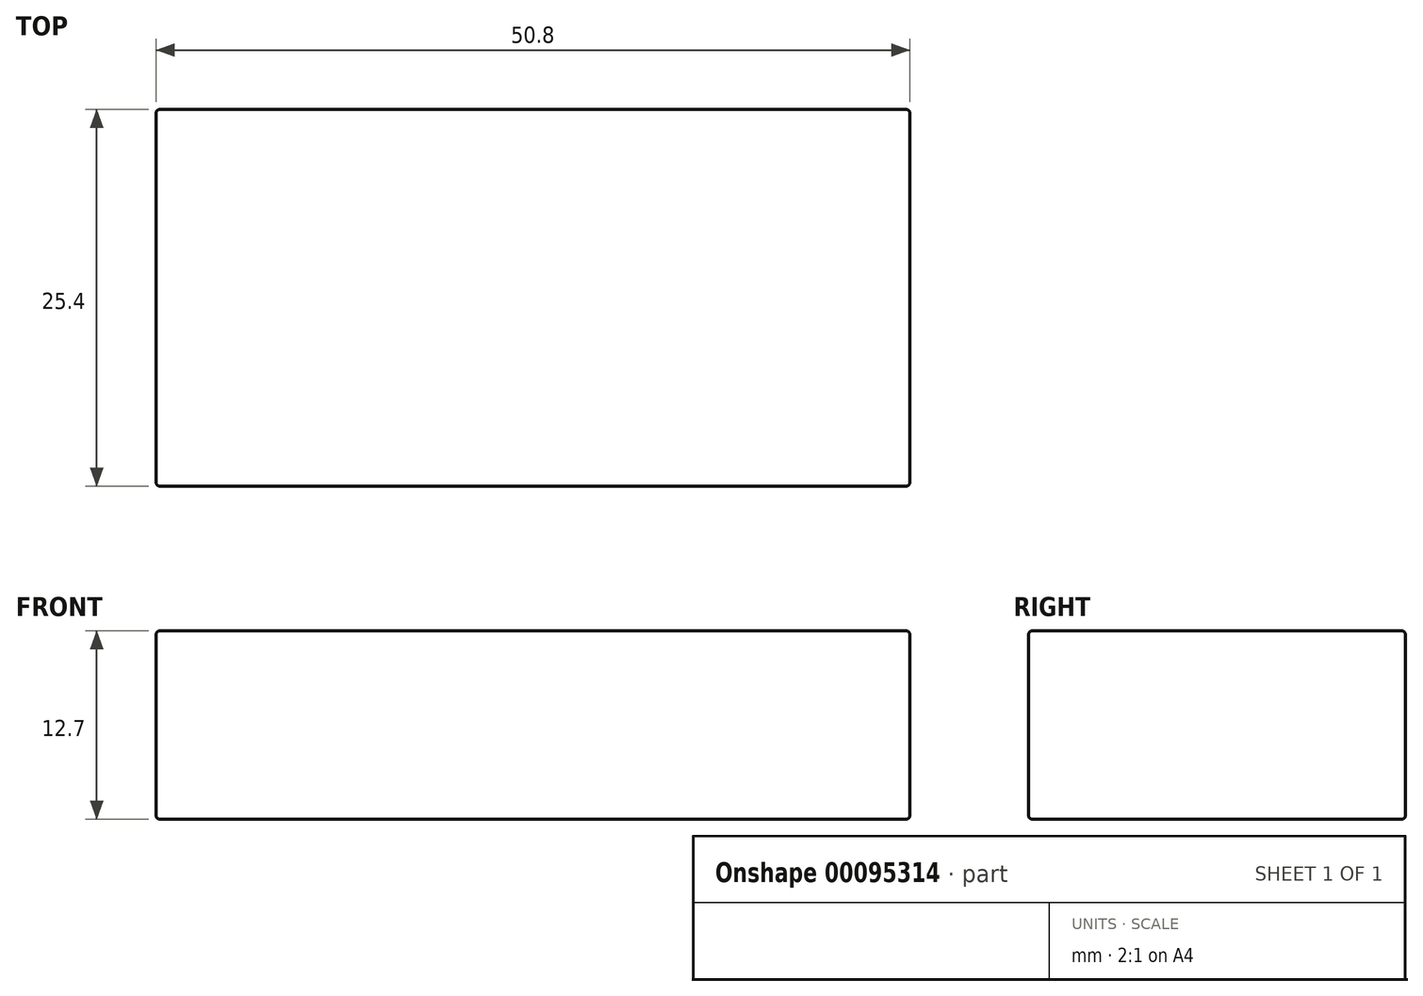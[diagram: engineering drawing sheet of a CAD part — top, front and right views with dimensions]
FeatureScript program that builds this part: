
annotation { "Feature Type Name" : "Feature", "Feature Type Description" : "" }
export const myFeature = defineFeature(function(context is Context, id is Id, definition is map)
    precondition{}
    {
        {
            var Q0;
            Q0=qCreatedBy(makeId("Front.planeOp"),FACE);
            var sketch = newSketch(context, id + "F0", { "sketchPlane" : qUnion([Q0])});
            skLineSegment(sketch, "E0.bottom", {"start": v(25.4, -6.35) * mm, "end": v(-25.4, -6.35) * mm});
            skLineSegment(sketch, "E0.top", {"start": v(25.4, 6.35) * mm, "end": v(-25.4, 6.35) * mm});
            skLineSegment(sketch, "E0.left", {"start": v(25.4, -6.35) * mm, "end": v(25.4, 6.35) * mm});
            skLineSegment(sketch, "E0.right", {"start": v(-25.4, -6.35) * mm, "end": v(-25.4, 6.35) * mm});
            skPoint(sketch, "E0.middle", {"position": v(0, 0) * mm});
            skSolve(sketch);
        }
        {
            var Q0;
            Q0=makeQuery(id+"F0.imprint","IMPRINT",FACE,{"disambiguationData":[TD([[makeQuery(id+"F0.imprint","IMPRINT",EDGE,{"derivedFrom":sQuery(id+"F0.wireOp",EDGE,"E0.bottom")}),-1.0]])]});
            extrude(context, id + "F1", {"entities" : qUnion([Q0]), "endBound" : BoundingType.SYMMETRIC, "depth" : 25.4 * mm});
        }
        {
            var Q0;
            Q0=makeQuery(id+"F1.opExtrude","SWEPT_FACE",FACE,{"disambiguationData":[OSD([sQuery(id+"F0.wireOp",EDGE,"E0.bottom")])]});
            var Q1;
            Q1=makeQuery(id+"F1.opExtrude","SWEPT_FACE",FACE,{"disambiguationData":[OSD([sQuery(id+"F0.wireOp",EDGE,"E0.top")])]});
            var Q2;
            Q2=makeQuery(id+"F1.opExtrude","SWEPT_FACE",FACE,{"disambiguationData":[OSD([sQuery(id+"F0.wireOp",EDGE,"E0.right")])]});
            var Q3;
            Q3=makeQuery(id+"F1.opExtrude","SWEPT_FACE",FACE,{"disambiguationData":[OSD([sQuery(id+"F0.wireOp",EDGE,"E0.left")])]});
            fillet(context, id + "F2", {"entities" : qUnion([Q0, Q1, Q2, Q3]), "radius" : 0.25 * mm, "tangentPropagation" : true, "allowEdgeOverflow" : false});
        }
    });
